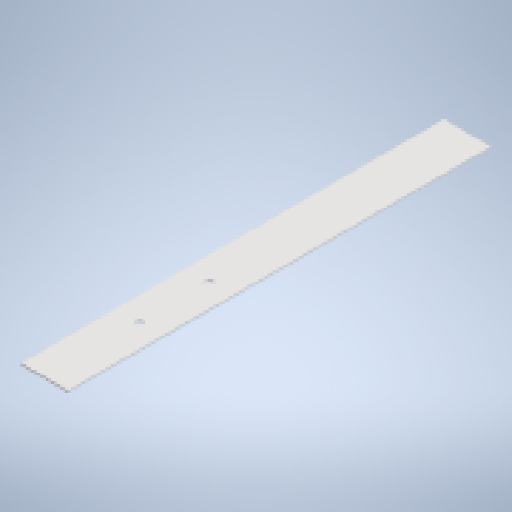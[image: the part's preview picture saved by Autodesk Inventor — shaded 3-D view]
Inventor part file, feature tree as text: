
AUTODESK INVENTOR PART (.ipt)
format: ipt  version: 2023 (Build 270158000, 158)  size: 141,312 bytes
history: native  units: mm
features: extrude x1, sketch x1
ambient origin geometry x8: Origin, YZ Plane, XZ Plane, XY Plane, X Axis, Y Axis, Z Axis, Center Point
bodies: Body1 (feature_tree)
feature tree (2):
  extrude  "Extrusion2"  Depth=450.0mm
  sketch  "Sketch1"  dims[d0=50.0mm d1=450.0mm d6=100.0mm d7=8.0mm d8=75.0mm d9=8.0mm d10=2.0mm d11=0.0mm]
